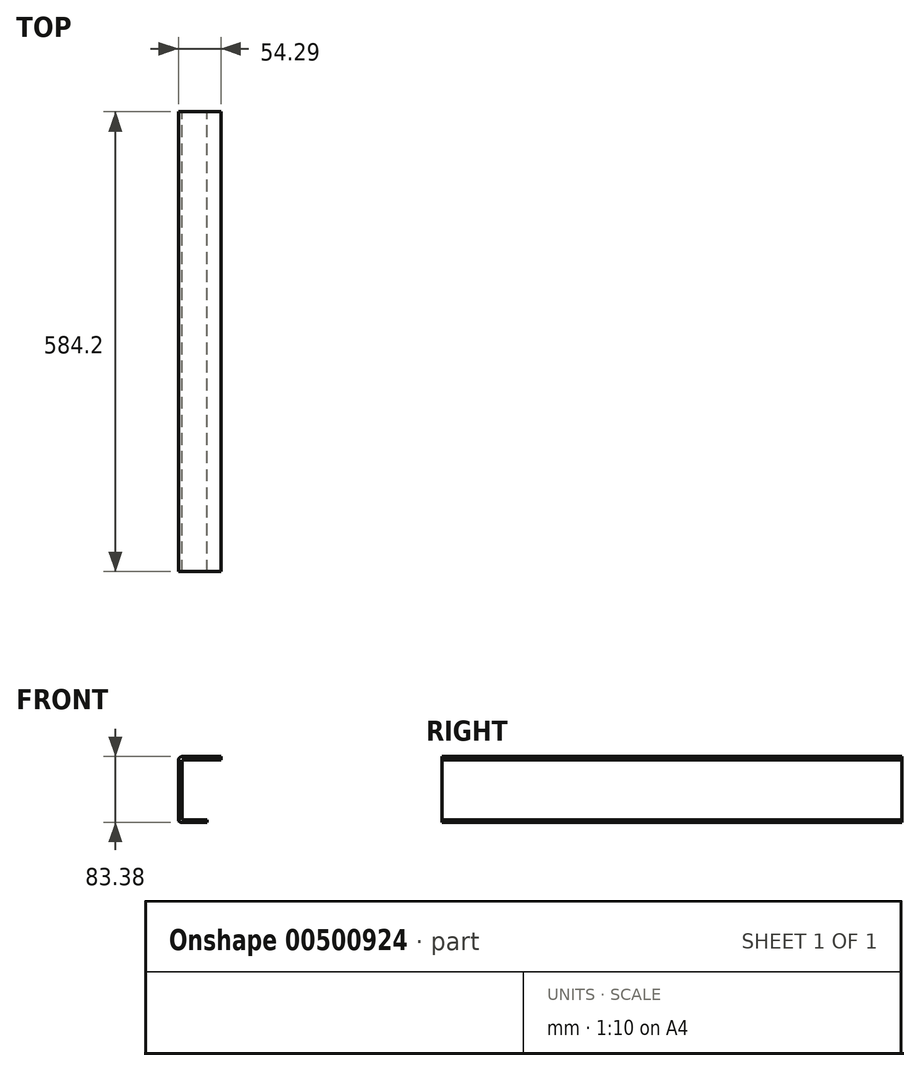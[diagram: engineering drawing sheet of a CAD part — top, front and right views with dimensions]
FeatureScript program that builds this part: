
annotation { "Feature Type Name" : "Feature", "Feature Type Description" : "" }
export const myFeature = defineFeature(function(context is Context, id is Id, definition is map)
    precondition{}
    {
        {
            var Q0;
            Q0=qCreatedBy(makeId("Right.planeOp"),FACE);
            var sketch = newSketch(context, id + "F0", { "sketchPlane" : qUnion([Q0])});
            skLineSegment(sketch, "E0.bottom", {"start": v(-97.95, 41.7) * mm, "end": v(97.95, 41.7) * mm});
            skLineSegment(sketch, "E0.top", {"start": v(-97.95, -41.7) * mm, "end": v(97.95, -41.7) * mm});
            skLineSegment(sketch, "E0.left", {"start": v(-97.95, 41.7) * mm, "end": v(-97.95, -41.7) * mm});
            skLineSegment(sketch, "E0.right", {"start": v(97.95, 41.7) * mm, "end": v(97.95, -41.7) * mm});
            skPoint(sketch, "E0.middle", {"position": v(0, 0) * mm});
            skSolve(sketch);
        }
        {
            var Q0;
            Q0=makeQuery(id+"F0.imprint","IMPRINT",FACE,{"disambiguationData":[TD([[makeQuery(id+"F0.imprint","IMPRINT",EDGE,{"derivedFrom":sQuery(id+"F0.wireOp",EDGE,"E0.bottom")}),-1.0]])]});
            extrude(context, id + "F1", {"entities" : qUnion([Q0]), "depth" : 4.76 * mm});
        }
        {
            var Q0;
            Q0=makeQuery(id+"F1.opExtrude","CAP_FACE",FACE,{"disambiguationData":[OSD([sQuery(id+"F0.wireOp",EDGE,"E0.bottom"),sQuery(id+"F0.wireOp",EDGE,"E0.top"),sQuery(id+"F0.wireOp",EDGE,"E0.left"),sQuery(id+"F0.wireOp",EDGE,"E0.right")])],"isStart":false});
            var sketch = newSketch(context, id + "F2", { "sketchPlane" : qUnion([Q0])});
            skLineSegment(sketch, "E1.bottom", {"start": v(-97.95, -41.7) * mm, "end": v(97.95, -41.7) * mm});
            skLineSegment(sketch, "E1.top", {"start": v(-97.95, -38.45) * mm, "end": v(97.95, -38.45) * mm});
            skLineSegment(sketch, "E1.left", {"start": v(-97.95, -41.7) * mm, "end": v(-97.95, -38.45) * mm});
            skLineSegment(sketch, "E1.right", {"start": v(97.95, -41.7) * mm, "end": v(97.95, -38.45) * mm});
            skSolve(sketch);
        }
        {
            var Q0;
            Q0=makeQuery(id+"F2.imprint","IMPRINT",FACE,{"disambiguationData":[TD([[makeQuery(id+"F2.imprint","IMPRINT",EDGE,{"derivedFrom":sQuery(id+"F2.wireOp",EDGE,"E1.bottom")}),1.0]])]});
            extrude(context, id + "F3", {"entities" : qUnion([Q0]), "operationType" : NewBodyOperationType.ADD, "depth" : 34.85 * mm});
        }
        {
            var Q0;
            Q0=makeQuery(id+"F1.opExtrude","CAP_EDGE",EDGE,{"disambiguationData":[OSD([sQuery(id+"F0.wireOp",EDGE,"E0.top")])],"isStart":true});
            fillet(context, id + "F4", {"entities" : qUnion([Q0]), "radius" : 3.68 * mm, "tangentPropagation" : true, "allowEdgeOverflow" : false});
        }
        {
            var Q0;
            Q0=makeQuery(id+"F3.opExtrude","CAP_FACE",FACE,{"disambiguationData":[OSD([sQuery(id+"F2.wireOp",EDGE,"E1.bottom"),sQuery(id+"F2.wireOp",EDGE,"E1.top"),sQuery(id+"F2.wireOp",EDGE,"E1.left"),sQuery(id+"F2.wireOp",EDGE,"E1.right")])],"isStart":false});
            extrude(context, id + "F5", {"entities" : qUnion([Q0]), "operationType" : NewBodyOperationType.REMOVE, "oppositeDirection" : true, "depth" : 3.17 * mm});
        }
        {
            var Q0;
            Q0=makeQuery(id+"F1.opExtrude","CAP_FACE",FACE,{"disambiguationData":[OSD([sQuery(id+"F0.wireOp",EDGE,"E0.bottom"),sQuery(id+"F0.wireOp",EDGE,"E0.top"),sQuery(id+"F0.wireOp",EDGE,"E0.left"),sQuery(id+"F0.wireOp",EDGE,"E0.right")])],"isStart":false});
            var sketch = newSketch(context, id + "F6", { "sketchPlane" : qUnion([Q0])});
            skLineSegment(sketch, "E2.bottom", {"start": v(-97.95, 41.7) * mm, "end": v(97.95, 41.7) * mm});
            skLineSegment(sketch, "E2.top", {"start": v(-97.95, 37.64) * mm, "end": v(97.95, 37.64) * mm});
            skLineSegment(sketch, "E2.left", {"start": v(-97.95, 41.7) * mm, "end": v(-97.95, 37.64) * mm});
            skLineSegment(sketch, "E2.right", {"start": v(97.95, 41.7) * mm, "end": v(97.95, 37.64) * mm});
            skSolve(sketch);
        }
        {
            var Q0;
            Q0=makeQuery(id+"F6.imprint","IMPRINT",FACE,{"disambiguationData":[TD([[makeQuery(id+"F6.imprint","IMPRINT",EDGE,{"derivedFrom":sQuery(id+"F6.wireOp",EDGE,"E2.bottom")}),-1.0]])]});
            extrude(context, id + "F7", {"entities" : qUnion([Q0]), "operationType" : NewBodyOperationType.ADD, "depth" : 49.53 * mm});
        }
        {
            var Q0;
            Q0=makeQuery(id+"F1.opExtrude","CAP_EDGE",EDGE,{"disambiguationData":[OSD([sQuery(id+"F0.wireOp",EDGE,"E0.bottom")])],"isStart":true});
            fillet(context, id + "F8", {"entities" : qUnion([Q0]), "radius" : 5.08 * mm, "tangentPropagation" : true, "allowEdgeOverflow" : false});
        }
        {
            var Q0;
            Q0=makeQuery(id+"F7.boolean.opBoolean","MERGE",FACE,{"derivedFrom":[makeQuery(id+"F3.boolean.opBoolean","MERGE",FACE,{"derivedFrom":[makeQuery(id+"F1.opExtrude","SWEPT_FACE",FACE,{"disambiguationData":[OSD([sQuery(id+"F0.wireOp",EDGE,"E0.right")])]}),makeQuery(id+"F3.opExtrude","SWEPT_FACE",FACE,{"disambiguationData":[OSD([sQuery(id+"F2.wireOp",EDGE,"E1.right")])]})]}),makeQuery(id+"F7.opExtrude","SWEPT_FACE",FACE,{"disambiguationData":[OSD([sQuery(id+"F6.wireOp",EDGE,"E2.right")])]})]});
            extrude(context, id + "F9", {"entities" : qUnion([Q0]), "operationType" : NewBodyOperationType.ADD, "depth" : 317.5 * mm});
        }
        {
            var Q0;
            Q0=makeQuery(id+"F7.boolean.opBoolean","MERGE",FACE,{"derivedFrom":[makeQuery(id+"F3.boolean.opBoolean","MERGE",FACE,{"derivedFrom":[makeQuery(id+"F1.opExtrude","SWEPT_FACE",FACE,{"disambiguationData":[OSD([sQuery(id+"F0.wireOp",EDGE,"E0.left")])]}),makeQuery(id+"F3.opExtrude","SWEPT_FACE",FACE,{"disambiguationData":[OSD([sQuery(id+"F2.wireOp",EDGE,"E1.left")])]})]}),makeQuery(id+"F7.opExtrude","SWEPT_FACE",FACE,{"disambiguationData":[OSD([sQuery(id+"F6.wireOp",EDGE,"E2.left")])]})]});
            extrude(context, id + "F10", {"entities" : qUnion([Q0]), "operationType" : NewBodyOperationType.ADD, "depth" : 317.5 * mm});
        }
        {
            var Q0;
            Q0=makeQuery(id+"F9.opExtrude","CAP_FACE",FACE,{"disambiguationData":[OSD([sQuery(id+"F0.wireOp",EDGE,"E0.right"),sQuery(id+"F2.wireOp",EDGE,"E1.right"),sQuery(id+"F6.wireOp",EDGE,"E2.right")])],"isStart":false});
            extrude(context, id + "F11", {"entities" : qUnion([Q0]), "operationType" : NewBodyOperationType.REMOVE, "oppositeDirection" : true, "depth" : 123.36 * mm});
        }
        {
            var Q0;
            Q0=makeQuery(id+"F10.opExtrude","CAP_FACE",FACE,{"disambiguationData":[OSD([sQuery(id+"F0.wireOp",EDGE,"E0.left"),sQuery(id+"F2.wireOp",EDGE,"E1.left"),sQuery(id+"F6.wireOp",EDGE,"E2.left")])],"isStart":false});
            extrude(context, id + "F12", {"entities" : qUnion([Q0]), "operationType" : NewBodyOperationType.REMOVE, "oppositeDirection" : true, "depth" : 123.36 * mm});
        }
    });
